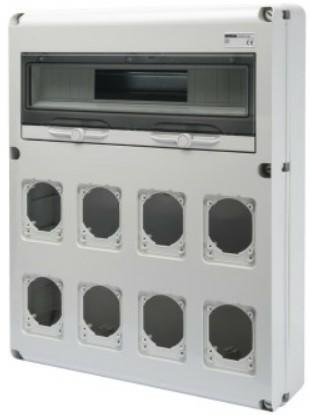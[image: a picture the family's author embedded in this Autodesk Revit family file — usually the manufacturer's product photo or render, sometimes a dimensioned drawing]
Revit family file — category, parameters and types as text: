
# Revit family: Building-IEC309Boards-GEWISS-68QDIN-DISTRIBUTION-BOARD-20MOD_8SOCKET-OUTLETS
name_source: partatom
category: Apparecchi elettrici
units: mm (PartAtom-declared; Revit-internal decimal feet)

## family parameters
Condiviso = No
Host = Superficie
Mantenere orientamento annotazione = Sì
Punto di calcolo locali = Sì
Quota connettore circolare = Usa diametro
Taglio con vuoti quando caricato = No
Tipo di parte = Normale

## types (1)
- GW68013N - Q-DIN 20M 8 FLANGES S.O.16/32A IP65
    Accordance with Standards = EN 60208 - EN 60670-1 - IEC 60670-24
    Catalogue = BUILDING
    Catalogue Range = 68 QDIN
    Colour = Grey RAL 7035
    Descrizione = Q-DIN 20M 8 FLANGES S.O.16/32A IP65
    Dispersible power A (W) = 30
    Dispersible power B (W) = 92
    EAN code = 8011564744905
    Electrocod = 2242
    Glow Wire Test = 650°C
    Houseable socket = 8 IEC 309 16/32A IP44/67
    IDF = 932c51f8-d567-42c7-b29d-d2d051754dad
    IDT = 3b58a0f8-96cf-43f3-8e98-bcad634a41cb
    IP degree = IP65
    Immagine tipo = GW68013N.jpg
    Installation type = Surface-mounting
    Insulation class = II
    L_Moduli = 380 mm  [stored 1.24672 ft]
    Modello = GW68013N
    N_Moduli = 20 mm  [stored 0.0656168 ft]
    No. of modules EN 50022 = 20
    No. of provided blank lids = 2 IEC 16/32A
    Operating temperature: = -25 +40 °C
    POMELLO = bianco
    PRESA = rosso
    Produttore = GEWISS S.p.A.
    Prospetto di default = 1219 mm
    SEO = Board
    STRUTTURA = RAL - 7035
    STRUTTURA ALTA = Poche
    Shock resistance = IK08
    Spostamento_S = 1000 mm  [stored 3.28084 ft]
    Technical sheet = https://www.gewiss.com
    Thermo-pressure with ball = 70
    URL = https://www.gewiss.com
    VETRO = Vetro
    Version file RFA = 21.5
    Version type = Empty

note: source unit labels omitted for Thermo-pressure with ball — the stored unit's dimension contradicts the parameter name (converter mislabeling)

note: [stored X ft] marks values corroborated as IEEE doubles in the binary element streams (Revit-internal decimal feet)

## geometry (parser evidence)
native form markers: Sweep x3
no freeform markers — native parametric forms only
